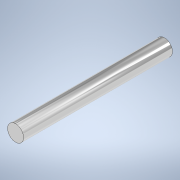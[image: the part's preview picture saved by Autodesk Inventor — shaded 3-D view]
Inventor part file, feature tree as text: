
AUTODESK INVENTOR PART (.ipt)
format: ipt  version: 2022 (Build 260153000, 153)  size: 98,304 bytes
history: native  units: mm
features: extrude x1, sketch x1
ambient origin geometry x8: Origin, YZ Plane, XZ Plane, XY Plane, X Axis, Y Axis, Z Axis, Center Point
bodies: Solid1 (feature_tree)
feature tree (2):
  extrude  "Extrusion1"  Depth=50.0mm TaperAngle=0.0deg
  sketch  "Sketch1"  dims[d0=5.4mm d1=50.0mm d2=0.0mm]
